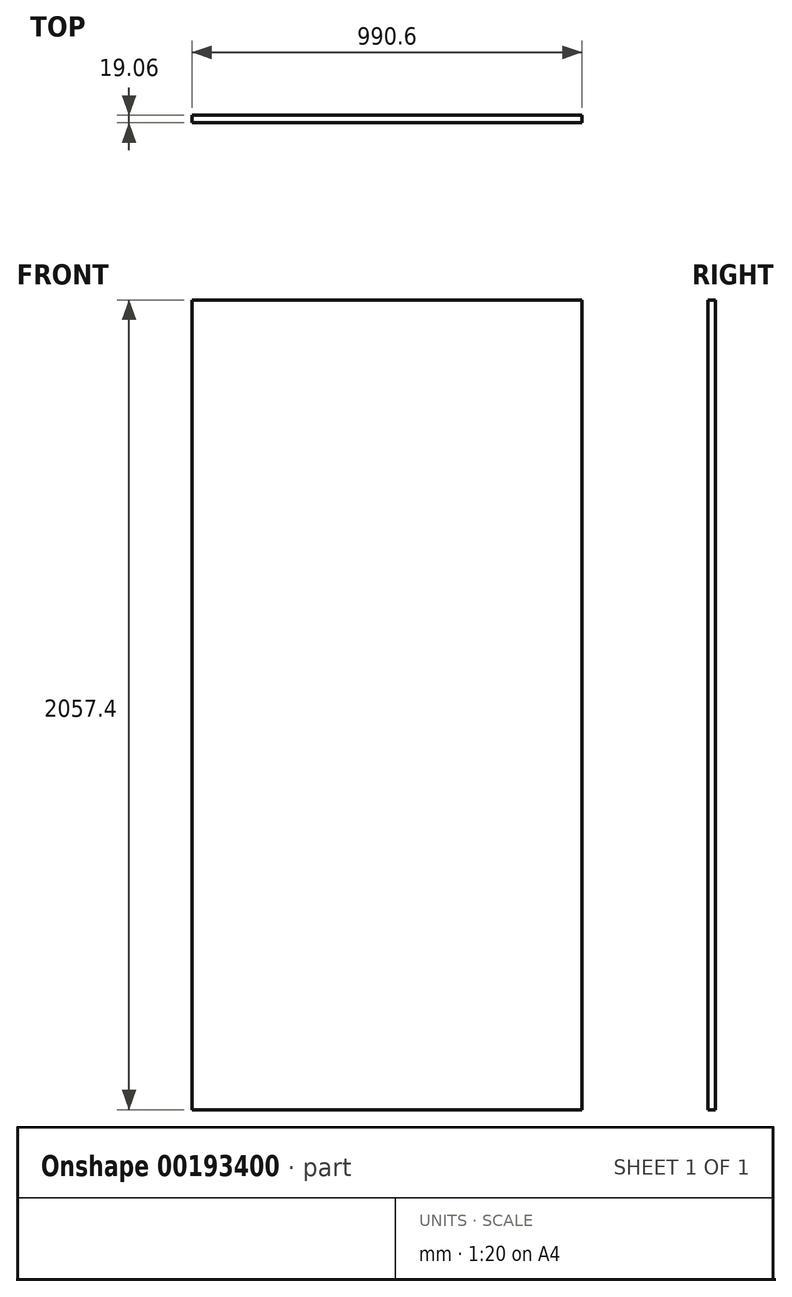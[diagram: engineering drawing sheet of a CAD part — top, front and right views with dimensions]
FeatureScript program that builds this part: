
annotation { "Feature Type Name" : "Feature", "Feature Type Description" : "" }
export const myFeature = defineFeature(function(context is Context, id is Id, definition is map)
    precondition{}
    {
        {
            var Q0;
            Q0=qCreatedBy(makeId("Front.planeOp"),FACE);
            var sketch = newSketch(context, id + "F0", { "sketchPlane" : qUnion([Q0])});
            skLineSegment(sketch, "E0.bottom", {"start": v(-495.3, 1028.7) * mm, "end": v(495.3, 1028.7) * mm});
            skLineSegment(sketch, "E0.top", {"start": v(-495.3, -1028.7) * mm, "end": v(495.3, -1028.7) * mm});
            skLineSegment(sketch, "E0.left", {"start": v(-495.3, 1028.7) * mm, "end": v(-495.3, -1028.7) * mm});
            skLineSegment(sketch, "E0.right", {"start": v(495.3, 1028.7) * mm, "end": v(495.3, -1028.7) * mm});
            skPoint(sketch, "E0.middle", {"position": v(0, 0) * mm});
            skSolve(sketch);
        }
        {
            var Q0;
            Q0 = qSketchRegion(id + "F0", true);
            extrude(context, id + "F1", {"entities" : qUnion([Q0]), "depth" : 19.05 * mm, "symmetric" : true});
        }
    });
